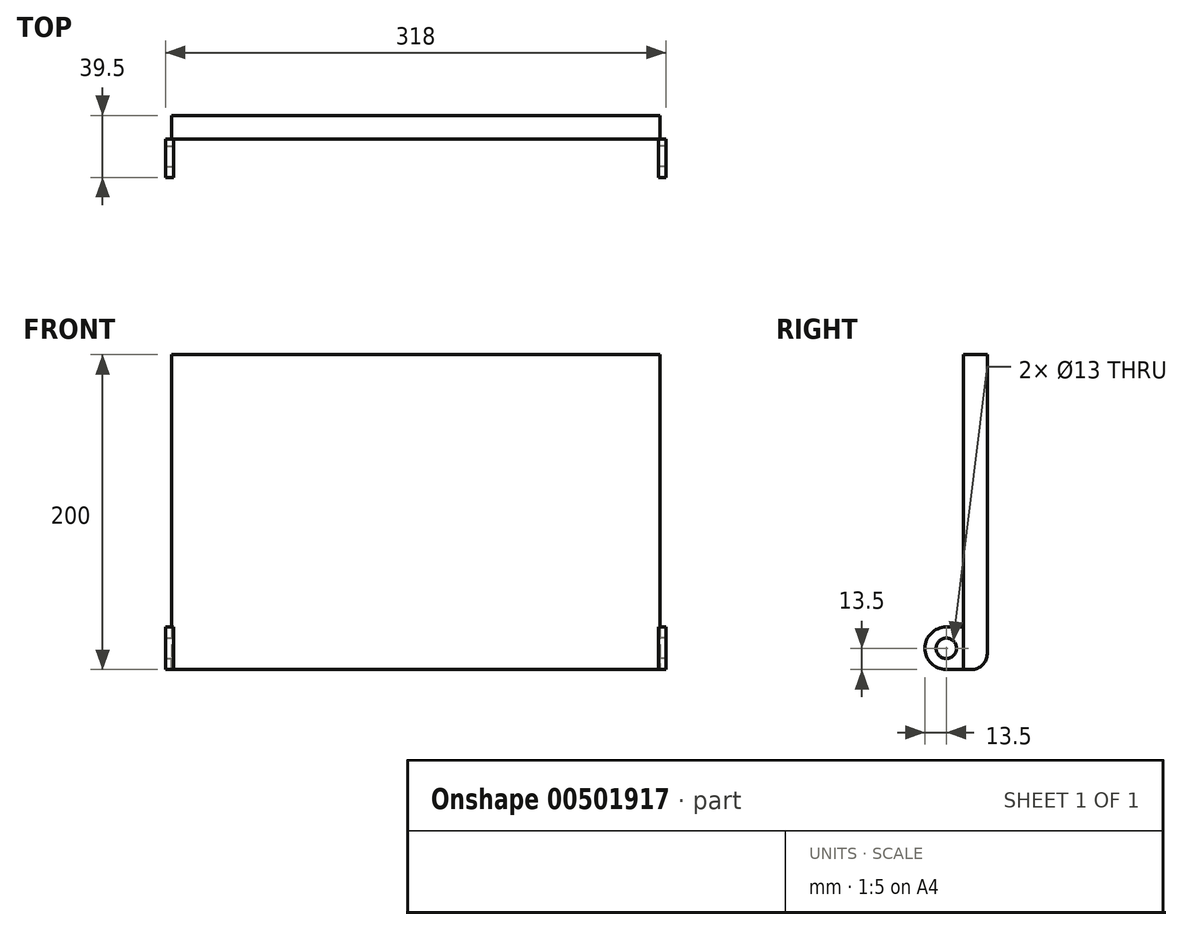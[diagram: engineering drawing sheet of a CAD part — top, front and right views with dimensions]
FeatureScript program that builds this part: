
annotation { "Feature Type Name" : "Feature", "Feature Type Description" : "" }
export const myFeature = defineFeature(function(context is Context, id is Id, definition is map)
    precondition{}
    {
        {
            var Q0;
            Q0=qCreatedBy(makeId("Front.planeOp"),FACE);
            var sketch = newSketch(context, id + "F0", { "sketchPlane" : qUnion([Q0])});
            skLineSegment(sketch, "E0.bottom", {"start": v(-155, 100) * mm, "end": v(155, 100) * mm});
            skLineSegment(sketch, "E0.top", {"start": v(-155, -100) * mm, "end": v(155, -100) * mm});
            skLineSegment(sketch, "E0.left", {"start": v(-155, 100) * mm, "end": v(-155, -100) * mm});
            skLineSegment(sketch, "E0.right", {"start": v(155, 100) * mm, "end": v(155, -100) * mm});
            skPoint(sketch, "E0.middle", {"position": v(0, 0) * mm});
            skSolve(sketch);
        }
        {
            var Q0;
            Q0=makeQuery(id+"F0.imprint","IMPRINT",FACE,{"disambiguationData":[TD([[makeQuery(id+"F0.imprint","IMPRINT",EDGE,{"derivedFrom":sQuery(id+"F0.wireOp",EDGE,"E0.bottom")}),-1.0]])]});
            extrude(context, id + "F1", {"entities" : qUnion([Q0]), "depth" : 15 * mm});
        }
        {
            var Q0;
            Q0=makeQuery(id+"F1.opExtrude","SWEPT_FACE",FACE,{"disambiguationData":[OSD([sQuery(id+"F0.wireOp",EDGE,"E0.right")])]});
            var sketch = newSketch(context, id + "F2", { "sketchPlane" : qUnion([Q0])});
            skLineSegment(sketch, "E1.bottom", {"start": v(-15, -100) * mm, "end": v(-26, -100) * mm});
            skLineSegment(sketch, "E1.top", {"start": v(-15, -73) * mm, "end": v(-26, -73) * mm});
            skLineSegment(sketch, "E1.left", {"start": v(-15, -100) * mm, "end": v(-15, -73) * mm});
            skArc(sketch, "E2", {"start": v(-26, -73) * mm, "mid": v(-39.5, -86.5) * mm, "end": v(-26, -100) * mm});
            skCircle(sketch, "E3", {"center": v(-26, -86.5) * mm, "radius": 6.5 * mm});
            skSolve(sketch);
        }
        {
            var Q0;
            Q0=makeQuery(id+"F1.opExtrude","CAP_EDGE",EDGE,{"disambiguationData":[OSD([sQuery(id+"F0.wireOp",EDGE,"E0.top")])],"isStart":true});
            fillet(context, id + "F3", {"entities" : qUnion([Q0]), "radius" : 10 * mm, "tangentPropagation" : true, "allowEdgeOverflow" : false});
        }
        {
            var Q0;
            Q0 = qSketchRegion(id + "F2", true);
            extrude(context, id + "F4", {"entities" : qUnion([Q0]), "operationType" : NewBodyOperationType.ADD, "depth" : 4 * mm, "hasSecondDirection" : true, "secondDirectionOppositeDirection" : true, "secondDirectionDepth" : 1 * mm});
        }
        {
            var Q0;
            Q0=makeQuery(id+"F1.opExtrude","SWEPT_FACE",FACE,{"disambiguationData":[OSD([sQuery(id+"F0.wireOp",EDGE,"E0.left")])]});
            var sketch = newSketch(context, id + "F5", { "sketchPlane" : qUnion([Q0])});
            skLineSegment(sketch, "E4.bottom", {"start": v(15, -73) * mm, "end": v(26, -73) * mm});
            skLineSegment(sketch, "E4.top", {"start": v(15, -100) * mm, "end": v(26, -100) * mm});
            skLineSegment(sketch, "E4.left", {"start": v(15, -73) * mm, "end": v(15, -100) * mm});
            skArc(sketch, "E5", {"start": v(26, -100) * mm, "mid": v(39.5, -86.5) * mm, "end": v(26, -73) * mm});
            skCircle(sketch, "E6", {"center": v(26, -86.5) * mm, "radius": 6.5 * mm});
            skSolve(sketch);
        }
        {
            var Q0;
            Q0 = qSketchRegion(id + "F5", true);
            extrude(context, id + "F6", {"entities" : qUnion([Q0]), "operationType" : NewBodyOperationType.ADD, "depth" : 4 * mm, "hasSecondDirection" : true, "secondDirectionOppositeDirection" : true, "secondDirectionDepth" : 1 * mm});
        }
    });
